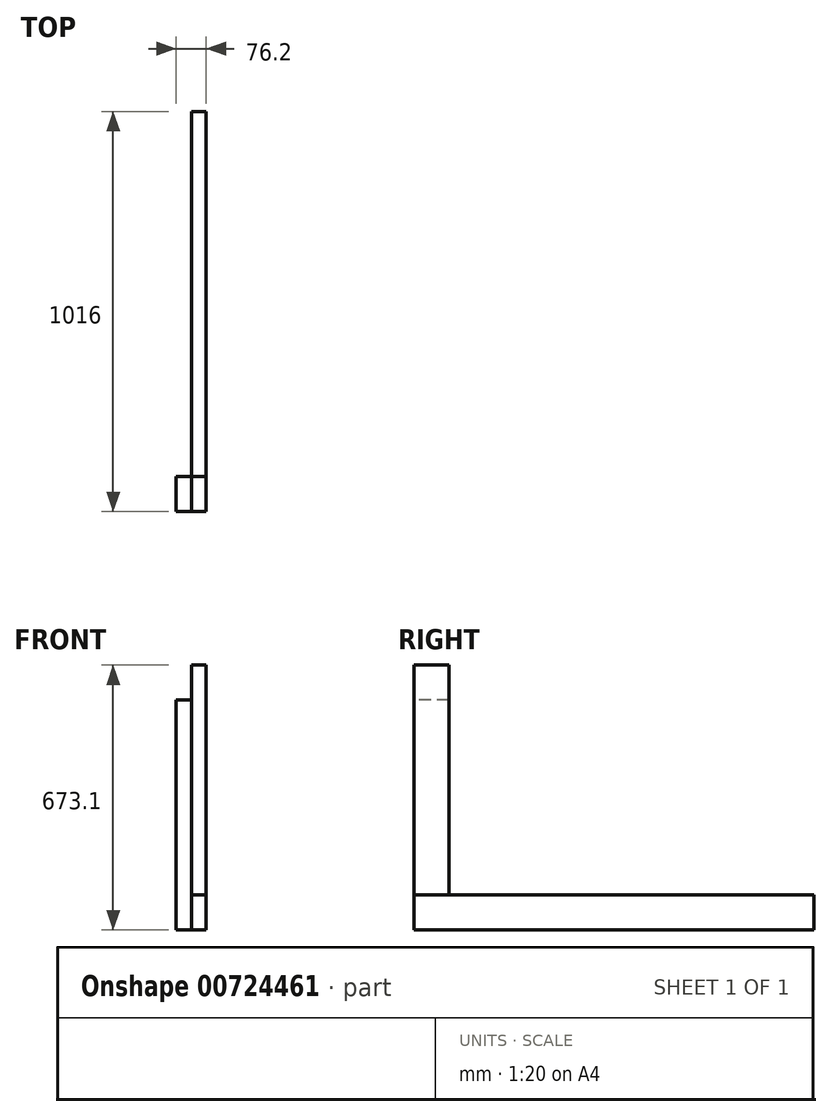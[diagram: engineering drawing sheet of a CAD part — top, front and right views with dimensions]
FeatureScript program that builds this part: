
annotation { "Feature Type Name" : "Feature", "Feature Type Description" : "" }
export const myFeature = defineFeature(function(context is Context, id is Id, definition is map)
    precondition{}
    {
        {
            var Q0;
            Q0=qCreatedBy(makeId("Front.planeOp"),FACE);
            var sketch = newSketch(context, id + "F0", { "sketchPlane" : qUnion([Q0])});
            skLineSegment(sketch, "E0", {"start": v(0, 0) * mm, "end": v(19.05, 0) * mm});
            skLineSegment(sketch, "E1", {"start": v(19.05, 0) * mm, "end": v(19.05, 88.9) * mm});
            skLineSegment(sketch, "E2", {"start": v(19.05, 88.9) * mm, "end": v(-19.05, 88.9) * mm});
            skLineSegment(sketch, "E3", {"start": v(-19.05, 88.9) * mm, "end": v(-19.05, 0) * mm});
            skLineSegment(sketch, "E4", {"start": v(-19.05, 0) * mm, "end": v(0, 0) * mm});
            skSolve(sketch);
        }
        {
            var Q0;
            Q0 = qSketchRegion(id + "F0", true);
            extrude(context, id + "F1", {"entities" : qUnion([Q0]), "oppositeDirection" : true, "depth" : 1016 * mm, "offsetDistance" : 25.4 * mm});
        }
        {
            var Q0;
            Q0=qCreatedBy(makeId("Top.planeOp"),FACE);
            var sketch = newSketch(context, id + "F2", { "sketchPlane" : qUnion([Q0])});
            skLineSegment(sketch, "E5.0.0", {"start": v(-19.05, 0) * mm, "end": v(19.05, 0) * mm});
            skLineSegment(sketch, "E5.0.1", {"start": v(19.05, 0) * mm, "end": v(19.05, 1016) * mm});
            skLineSegment(sketch, "E5.0.2", {"start": v(19.05, 1016) * mm, "end": v(-19.05, 1016) * mm});
            skLineSegment(sketch, "E5.0.3", {"start": v(-19.05, 1016) * mm, "end": v(-19.05, 0) * mm});
            skLineSegment(sketch, "E6.bottom", {"start": v(-19.05, 0) * mm, "end": v(-57.15, 0) * mm});
            skLineSegment(sketch, "E6.top", {"start": v(-19.05, 88.9) * mm, "end": v(-57.15, 88.9) * mm});
            skLineSegment(sketch, "E6.left", {"start": v(-19.05, 0) * mm, "end": v(-19.05, 88.9) * mm});
            skLineSegment(sketch, "E6.right", {"start": v(-57.15, 0) * mm, "end": v(-57.15, 88.9) * mm});
            skSolve(sketch);
        }
        {
            var Q0;
            Q0=makeQuery(id+"F2.imprint","IMPRINT",FACE,{"disambiguationData":[TD([[makeQuery(id+"F2.imprint","IMPRINT",EDGE,{"derivedFrom":sQuery(id+"F2.wireOp",EDGE,"E6.bottom")}),-1.0]])]});
            extrude(context, id + "F3", {"entities" : qUnion([Q0]), "depth" : 584.2 * mm, "offsetDistance" : 25.4 * mm});
        }
        {
            var Q0;
            Q0=makeQuery(id+"F1.opExtrude","SWEPT_FACE",FACE,{"disambiguationData":[OSD([sQuery(id+"F0.wireOp",EDGE,"E2")])]});
            var sketch = newSketch(context, id + "F4", { "sketchPlane" : qUnion([Q0])});
            skLineSegment(sketch, "E7.bottom", {"start": v(-19.05, 0) * mm, "end": v(19.05, 0) * mm});
            skLineSegment(sketch, "E7.top", {"start": v(-19.05, 88.9) * mm, "end": v(19.05, 88.9) * mm});
            skLineSegment(sketch, "E7.left", {"start": v(-19.05, 0) * mm, "end": v(-19.05, 88.9) * mm});
            skLineSegment(sketch, "E7.right", {"start": v(19.05, 0) * mm, "end": v(19.05, 88.9) * mm});
            skSolve(sketch);
        }
        {
            var Q0;
            Q0=makeQuery(id+"F4.imprint","IMPRINT",FACE,{"disambiguationData":[TD([[makeQuery(id+"F4.imprint","IMPRINT",EDGE,{"derivedFrom":sQuery(id+"F4.wireOp",EDGE,"E7.bottom")}),-1.0]])]});
            extrude(context, id + "F5", {"entities" : qUnion([Q0]), "depth" : 584.2 * mm, "offsetDistance" : 25.4 * mm});
        }
    });
